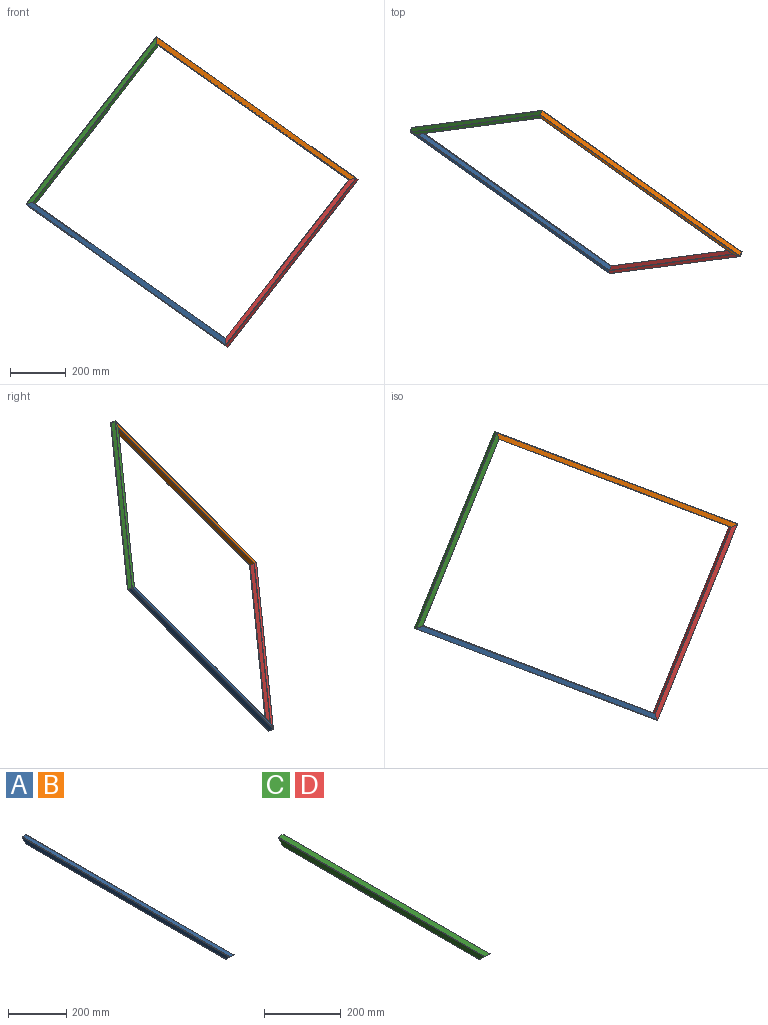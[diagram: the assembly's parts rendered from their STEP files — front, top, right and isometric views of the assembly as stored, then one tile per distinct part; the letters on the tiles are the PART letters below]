
ASSEMBLY  parts=4 mates=9
PART A: 14 faces, bbox 20x1010x20 mm
  f0: plane 1010x18mm, normal (0,0,1), area 18180mm2, adj f8,f9,f10,f13
  f1: plane 1008x18mm, normal (-1,0,0), area 17820mm2, adj f8,f9,f10,f11
  f2: plane 970x18mm, normal (0,0,-1), area 17460mm2, adj f8,f9,f11,f12
  f3: plane 1006x16mm, normal (-1,0,0), area 15840mm2, adj f4,f6,f8,f9
  f4: plane 974x16mm, normal (0,0,1), area 15584mm2, adj f3,f5,f8,f9
  f5: plane 1006x16mm, normal (1,0,0), area 15840mm2, adj f4,f6,f8,f9
  f6: plane 1006x16mm, normal (0,0,-1), area 16096mm2, adj f3,f5,f8,f9
  f7: plane 1008x18mm, normal (1,0,0), area 17820mm2, adj f8,f9,f12,f13
  f8: plane 20x20mm, normal (0,-0.71,-0.71), area 202.4mm2, adj f0,f1,f2,f3,f4,f5,f6,f7
  f9: plane 20x20mm, normal (0,0.71,-0.71), area 202.4mm2, adj f0,f1,f2,f3,f4,f5,f6,f7
  f10: cylinder r=1mm len=1010mm, axis (0,-1,0), area 1585.4mm2, adj f0,f1,f8,f9
  f11: cylinder r=1mm len=972mm, axis (0,1,0), area 1524.8mm2, adj f1,f2,f8,f9
  f12: cylinder r=1mm len=972mm, axis (0,-1,0), area 1524.8mm2, adj f2,f7,f8,f9
  f13: cylinder r=1mm len=1010mm, axis (0,1,0), area 1585.4mm2, adj f0,f7,f8,f9
PART B: same geometry as A
PART C: 14 faces, bbox 20x760x20 mm
  f0: plane 760x18mm, normal (0,0,1), area 13680mm2, adj f8,f9,f10,f13
  f1: plane 758x18mm, normal (-1,0,0), area 13320mm2, adj f8,f9,f10,f11
  f2: plane 720x18mm, normal (0,0,-1), area 12960mm2, adj f8,f9,f11,f12
  f3: plane 756x16mm, normal (-1,0,0), area 11840mm2, adj f4,f6,f8,f9
  f4: plane 724x16mm, normal (0,0,1), area 11584mm2, adj f3,f5,f8,f9
  f5: plane 756x16mm, normal (1,0,0), area 11840mm2, adj f4,f6,f8,f9
  f6: plane 756x16mm, normal (0,0,-1), area 12096mm2, adj f3,f5,f8,f9
  f7: plane 758x18mm, normal (1,0,0), area 13320mm2, adj f8,f9,f12,f13
  f8: plane 20x20mm, normal (0,-0.71,-0.71), area 202.4mm2, adj f0,f1,f2,f3,f4,f5,f6,f7
  f9: plane 20x20mm, normal (0,0.71,-0.71), area 202.4mm2, adj f0,f1,f2,f3,f4,f5,f6,f7
  f10: cylinder r=1mm len=760mm, axis (0,-1,0), area 1192.7mm2, adj f0,f1,f8,f9
  f11: cylinder r=1mm len=722mm, axis (0,1,0), area 1132.1mm2, adj f1,f2,f8,f9
  f12: cylinder r=1mm len=722mm, axis (0,-1,0), area 1132.1mm2, adj f2,f7,f8,f9
  f13: cylinder r=1mm len=760mm, axis (0,1,0), area 1192.7mm2, adj f0,f7,f8,f9
PART D: same geometry as C
PLACE A rot(axis=(0.51,-0.85,-0.14),145.1deg) t=(-871.68,-34.53,64.88)mm
PLACE B rot(axis=(-0.34,0.15,-0.93),122.2deg) t=(267.37,-460.73,161.94)mm
PLACE C rot(axis=(0.16,-0.58,-0.8),112.8deg) t=(-431.72,28.48,644.07)mm
PLACE D rot(axis=(-0.56,0.67,-0.49),165.1deg) t=(-172.59,-523.73,-417.25)mm
MATE planar C.f8 <-> A.f9  axis (0.07,-0.41,-0.91) through (-892.13,-33.06,70.49)mm
MATE planar B.f9 <-> D.f8  axis (0.07,-0.41,-0.91) through (274.44,-465.73,156.94)mm
MATE parallel D.f2 <-> C.f2  axis (-0.71,0.5,0.5) through (40.79,-490.13,-129.09)mm
MATE planar B.f1 <-> A.f1  axis (0.35,0.86,-0.36) through (-72.01,-209.6,400.86)mm
MATE planar A.f1 <-> D.f1  axis (0.35,0.86,-0.36) through (-525.23,-268.41,-181.29)mm
MATE planar B.f8 <-> C.f9  axis (-0.93,0.3,-0.2) through (-425.6,29.27,651.94)mm
MATE parallel A.f2 <-> B.f2  axis (0.61,0.08,0.79) through (-522.61,-276.23,-169.75)mm
MATE planar A.f9 <-> C.f8  axis (-0.07,0.41,0.91) through (-878.75,-29.53,69.88)mm
MATE planar D.f1 <-> C.f1  axis (0.35,0.86,-0.36) through (51.45,-486.54,-137.75)mm
